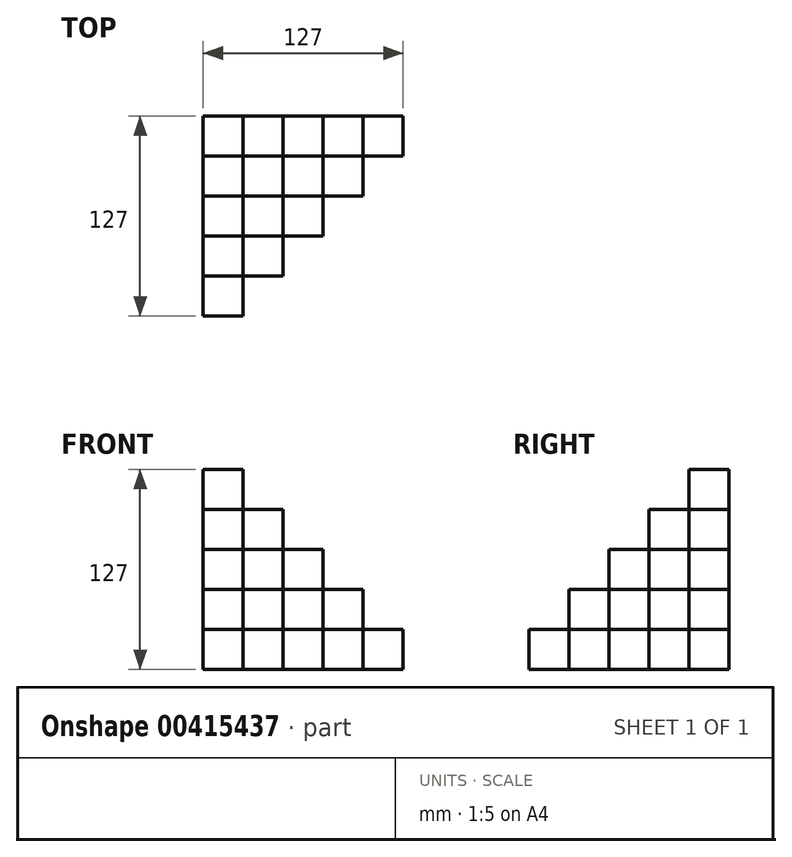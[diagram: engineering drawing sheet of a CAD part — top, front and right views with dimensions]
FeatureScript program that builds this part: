
annotation { "Feature Type Name" : "Feature", "Feature Type Description" : "" }
export const myFeature = defineFeature(function(context is Context, id is Id, definition is map)
    precondition{}
    {
        {
            var Q0;
            Q0=qCreatedBy(makeId("Top.planeOp"),FACE);
            var sketch = newSketch(context, id + "F0", { "sketchPlane" : qUnion([Q0])});
            skLineSegment(sketch, "E0.bottom", {"start": v(63.5, 63.5) * mm, "end": v(-63.5, 63.5) * mm, "construction": true});
            skLineSegment(sketch, "E0.top", {"start": v(63.5, -63.5) * mm, "end": v(-63.5, -63.5) * mm, "construction": true});
            skLineSegment(sketch, "E0.left", {"start": v(63.5, 63.5) * mm, "end": v(63.5, -63.5) * mm, "construction": true});
            skLineSegment(sketch, "E0.right", {"start": v(-63.5, 63.5) * mm, "end": v(-63.5, -63.5) * mm, "construction": true});
            skPoint(sketch, "E0.middle", {"position": v(0, 0) * mm});
            skLineSegment(sketch, "E1.bottom", {"start": v(-63.5, -63.5) * mm, "end": v(-38.1, -63.5) * mm});
            skLineSegment(sketch, "E1.top", {"start": v(-63.5, -38.1) * mm, "end": v(-38.1, -38.1) * mm});
            skLineSegment(sketch, "E1.left", {"start": v(-63.5, -63.5) * mm, "end": v(-63.5, -38.1) * mm});
            skLineSegment(sketch, "E1.right", {"start": v(-38.1, -63.5) * mm, "end": v(-38.1, -38.1) * mm});
            skLineSegment(sketch, "E2.bottom", {"start": v(-38.1, -38.1) * mm, "end": v(-12.7, -38.1) * mm});
            skLineSegment(sketch, "E2.top", {"start": v(-38.1, -12.7) * mm, "end": v(-12.7, -12.7) * mm});
            skLineSegment(sketch, "E2.left", {"start": v(-38.1, -38.1) * mm, "end": v(-38.1, -12.7) * mm});
            skLineSegment(sketch, "E2.right", {"start": v(-12.7, -38.1) * mm, "end": v(-12.7, -12.7) * mm});
            skLineSegment(sketch, "E3.bottom", {"start": v(-12.7, -12.7) * mm, "end": v(12.7, -12.7) * mm});
            skLineSegment(sketch, "E3.top", {"start": v(-12.7, 12.7) * mm, "end": v(12.7, 12.7) * mm});
            skLineSegment(sketch, "E3.left", {"start": v(-12.7, -12.7) * mm, "end": v(-12.7, 12.7) * mm});
            skLineSegment(sketch, "E3.right", {"start": v(12.7, -12.7) * mm, "end": v(12.7, 12.7) * mm});
            skLineSegment(sketch, "E4.bottom", {"start": v(12.7, 12.7) * mm, "end": v(38.1, 12.7) * mm});
            skLineSegment(sketch, "E4.top", {"start": v(12.7, 38.1) * mm, "end": v(38.1, 38.1) * mm});
            skLineSegment(sketch, "E4.left", {"start": v(12.7, 12.7) * mm, "end": v(12.7, 38.1) * mm});
            skLineSegment(sketch, "E4.right", {"start": v(38.1, 12.7) * mm, "end": v(38.1, 38.1) * mm});
            skLineSegment(sketch, "E5.bottom", {"start": v(38.1, 38.1) * mm, "end": v(63.5, 38.1) * mm});
            skLineSegment(sketch, "E5.top", {"start": v(38.1, 63.5) * mm, "end": v(63.5, 63.5) * mm});
            skLineSegment(sketch, "E5.left", {"start": v(38.1, 38.1) * mm, "end": v(38.1, 63.5) * mm});
            skLineSegment(sketch, "E5.right", {"start": v(63.5, 38.1) * mm, "end": v(63.5, 63.5) * mm});
            skSolve(sketch);
        }
        {
            var Q0;
            Q0=makeQuery(id+"F0.imprint","IMPRINT",FACE,{"disambiguationData":[TD([[makeQuery(id+"F0.imprint","IMPRINT",EDGE,{"derivedFrom":sQuery(id+"F0.wireOp",EDGE,"E2.bottom")}),1.0]])]});
            var Q1;
            Q1=makeQuery(id+"F0.imprint","IMPRINT",FACE,{"disambiguationData":[TD([[makeQuery(id+"F0.imprint","IMPRINT",EDGE,{"derivedFrom":sQuery(id+"F0.wireOp",EDGE,"E1.bottom")}),1.0]])]});
            var Q2;
            Q2=makeQuery(id+"F0.imprint","IMPRINT",FACE,{"disambiguationData":[TD([[makeQuery(id+"F0.imprint","IMPRINT",EDGE,{"derivedFrom":sQuery(id+"F0.wireOp",EDGE,"E3.bottom")}),1.0]])]});
            var Q3;
            Q3=makeQuery(id+"F0.imprint","IMPRINT",FACE,{"disambiguationData":[TD([[makeQuery(id+"F0.imprint","IMPRINT",EDGE,{"derivedFrom":sQuery(id+"F0.wireOp",EDGE,"E4.bottom")}),1.0]])]});
            var Q4;
            Q4=makeQuery(id+"F0.imprint","IMPRINT",FACE,{"disambiguationData":[TD([[makeQuery(id+"F0.imprint","IMPRINT",EDGE,{"derivedFrom":sQuery(id+"F0.wireOp",EDGE,"E5.bottom")}),1.0]])]});
            extrude(context, id + "F1", {"entities" : qUnion([Q0, Q1, Q2, Q3, Q4]), "depth" : 25.4 * mm});
        }
        {
            var Q0;
            Q0=qCreatedBy(makeId("Top.planeOp"),FACE);
            var sketch = newSketch(context, id + "F2", { "sketchPlane" : qUnion([Q0])});
            skLineSegment(sketch, "E6.bottom", {"start": v(63.5, 63.5) * mm, "end": v(-63.5, 63.5) * mm, "construction": true});
            skLineSegment(sketch, "E6.top", {"start": v(63.5, -63.5) * mm, "end": v(-63.5, -63.5) * mm, "construction": true});
            skLineSegment(sketch, "E6.left", {"start": v(63.5, 63.5) * mm, "end": v(63.5, -63.5) * mm, "construction": true});
            skLineSegment(sketch, "E6.right", {"start": v(-63.5, 63.5) * mm, "end": v(-63.5, -63.5) * mm, "construction": true});
            skPoint(sketch, "E6.middle", {"position": v(0, 0) * mm});
            skLineSegment(sketch, "E7", {"start": v(-63.5, -63.5) * mm, "end": v(-63.5, -38.1) * mm, "construction": true});
            skLineSegment(sketch, "E8", {"start": v(63.5, 63.5) * mm, "end": v(38.1, 63.5) * mm, "construction": true});
            skLineSegment(sketch, "E9.bottom", {"start": v(-63.5, -38.1) * mm, "end": v(-38.1, -38.1) * mm});
            skLineSegment(sketch, "E9.top", {"start": v(-63.5, -12.7) * mm, "end": v(-38.1, -12.7) * mm});
            skLineSegment(sketch, "E9.left", {"start": v(-63.5, -38.1) * mm, "end": v(-63.5, -12.7) * mm});
            skLineSegment(sketch, "E9.right", {"start": v(-38.1, -38.1) * mm, "end": v(-38.1, -12.7) * mm});
            skLineSegment(sketch, "E10.bottom", {"start": v(-38.1, -12.7) * mm, "end": v(-12.7, -12.7) * mm});
            skLineSegment(sketch, "E10.top", {"start": v(-38.1, 12.7) * mm, "end": v(-12.7, 12.7) * mm});
            skLineSegment(sketch, "E10.left", {"start": v(-38.1, -12.7) * mm, "end": v(-38.1, 12.7) * mm});
            skLineSegment(sketch, "E10.right", {"start": v(-12.7, -12.7) * mm, "end": v(-12.7, 12.7) * mm});
            skLineSegment(sketch, "E11.bottom", {"start": v(-12.7, 12.7) * mm, "end": v(12.7, 12.7) * mm});
            skLineSegment(sketch, "E11.top", {"start": v(-12.7, 38.1) * mm, "end": v(12.7, 38.1) * mm});
            skLineSegment(sketch, "E11.left", {"start": v(-12.7, 12.7) * mm, "end": v(-12.7, 38.1) * mm});
            skLineSegment(sketch, "E11.right", {"start": v(12.7, 12.7) * mm, "end": v(12.7, 38.1) * mm});
            skLineSegment(sketch, "E12.bottom", {"start": v(12.7, 38.1) * mm, "end": v(38.1, 38.1) * mm});
            skLineSegment(sketch, "E12.top", {"start": v(12.7, 63.5) * mm, "end": v(38.1, 63.5) * mm});
            skLineSegment(sketch, "E12.left", {"start": v(12.7, 38.1) * mm, "end": v(12.7, 63.5) * mm});
            skLineSegment(sketch, "E12.right", {"start": v(38.1, 38.1) * mm, "end": v(38.1, 63.5) * mm});
            skSolve(sketch);
        }
        {
            var Q0;
            Q0=qSketchRegion(id+"F2",true);
            extrude(context, id + "F3", {"entities" : qUnion([Q0]), "depth" : 50.8 * mm});
        }
        {
            var Q0;
            Q0=qCreatedBy(makeId("Top.planeOp"),FACE);
            var sketch = newSketch(context, id + "F4", { "sketchPlane" : qUnion([Q0])});
            skLineSegment(sketch, "E13.bottom", {"start": v(63.5, 63.5) * mm, "end": v(-63.5, 63.5) * mm, "construction": true});
            skLineSegment(sketch, "E13.top", {"start": v(63.5, -63.5) * mm, "end": v(-63.5, -63.5) * mm, "construction": true});
            skLineSegment(sketch, "E13.left", {"start": v(63.5, 63.5) * mm, "end": v(63.5, -63.5) * mm, "construction": true});
            skLineSegment(sketch, "E13.right", {"start": v(-63.5, 63.5) * mm, "end": v(-63.5, -63.5) * mm, "construction": true});
            skPoint(sketch, "E13.middle", {"position": v(0, 0) * mm});
            skLineSegment(sketch, "E14", {"start": v(-63.5, -63.5) * mm, "end": v(-63.5, -12.7) * mm, "construction": true});
            skLineSegment(sketch, "E15", {"start": v(63.5, 63.5) * mm, "end": v(12.7, 63.5) * mm, "construction": true});
            skLineSegment(sketch, "E16.bottom", {"start": v(12.7, 63.5) * mm, "end": v(-12.7, 63.5) * mm});
            skLineSegment(sketch, "E16.top", {"start": v(12.7, 38.1) * mm, "end": v(-12.7, 38.1) * mm});
            skLineSegment(sketch, "E16.left", {"start": v(12.7, 63.5) * mm, "end": v(12.7, 38.1) * mm});
            skLineSegment(sketch, "E16.right", {"start": v(-12.7, 63.5) * mm, "end": v(-12.7, 38.1) * mm});
            skLineSegment(sketch, "E17.bottom", {"start": v(-12.7, 38.1) * mm, "end": v(-38.1, 38.1) * mm});
            skLineSegment(sketch, "E17.top", {"start": v(-12.7, 12.7) * mm, "end": v(-38.1, 12.7) * mm});
            skLineSegment(sketch, "E17.left", {"start": v(-12.7, 38.1) * mm, "end": v(-12.7, 12.7) * mm});
            skLineSegment(sketch, "E17.right", {"start": v(-38.1, 38.1) * mm, "end": v(-38.1, 12.7) * mm});
            skLineSegment(sketch, "E18.bottom", {"start": v(-38.1, 12.7) * mm, "end": v(-63.5, 12.7) * mm});
            skLineSegment(sketch, "E18.top", {"start": v(-38.1, -12.7) * mm, "end": v(-63.5, -12.7) * mm});
            skLineSegment(sketch, "E18.left", {"start": v(-38.1, 12.7) * mm, "end": v(-38.1, -12.7) * mm});
            skLineSegment(sketch, "E18.right", {"start": v(-63.5, 12.7) * mm, "end": v(-63.5, -12.7) * mm});
            skSolve(sketch);
        }
        {
            var Q0;
            Q0=makeQuery(id+"F4.imprint","IMPRINT",FACE,{"disambiguationData":[TD([[makeQuery(id+"F4.imprint","IMPRINT",EDGE,{"derivedFrom":sQuery(id+"F4.wireOp",EDGE,"E18.bottom")}),1.0]])]});
            var Q1;
            Q1=makeQuery(id+"F4.imprint","IMPRINT",FACE,{"disambiguationData":[TD([[makeQuery(id+"F4.imprint","IMPRINT",EDGE,{"derivedFrom":sQuery(id+"F4.wireOp",EDGE,"E17.bottom")}),1.0]])]});
            var Q2;
            Q2=makeQuery(id+"F4.imprint","IMPRINT",FACE,{"disambiguationData":[TD([[makeQuery(id+"F4.imprint","IMPRINT",EDGE,{"derivedFrom":sQuery(id+"F4.wireOp",EDGE,"E16.bottom")}),1.0]])]});
            extrude(context, id + "F5", {"entities" : qUnion([Q0, Q1, Q2]), "depth" : 76.2 * mm});
        }
        {
            var Q0;
            Q0=qCreatedBy(makeId("Top.planeOp"),FACE);
            var sketch = newSketch(context, id + "F6", { "sketchPlane" : qUnion([Q0])});
            skLineSegment(sketch, "E19.bottom", {"start": v(63.5, 63.5) * mm, "end": v(-63.5, 63.5) * mm, "construction": true});
            skLineSegment(sketch, "E19.top", {"start": v(63.5, -63.5) * mm, "end": v(-63.5, -63.5) * mm, "construction": true});
            skLineSegment(sketch, "E19.left", {"start": v(63.5, 63.5) * mm, "end": v(63.5, -63.5) * mm, "construction": true});
            skLineSegment(sketch, "E19.right", {"start": v(-63.5, 63.5) * mm, "end": v(-63.5, -63.5) * mm, "construction": true});
            skPoint(sketch, "E19.middle", {"position": v(0, 0) * mm});
            skLineSegment(sketch, "E20", {"start": v(-63.5, 63.5) * mm, "end": v(-63.5, 12.7) * mm, "construction": true});
            skLineSegment(sketch, "E21", {"start": v(-63.5, 63.5) * mm, "end": v(-12.7, 63.5) * mm, "construction": true});
            skLineSegment(sketch, "E22.bottom", {"start": v(-63.5, 12.7) * mm, "end": v(-38.1, 12.7) * mm});
            skLineSegment(sketch, "E22.top", {"start": v(-63.5, 38.1) * mm, "end": v(-38.1, 38.1) * mm});
            skLineSegment(sketch, "E22.left", {"start": v(-63.5, 12.7) * mm, "end": v(-63.5, 38.1) * mm});
            skLineSegment(sketch, "E22.right", {"start": v(-38.1, 12.7) * mm, "end": v(-38.1, 38.1) * mm});
            skLineSegment(sketch, "E23.bottom", {"start": v(-38.1, 38.1) * mm, "end": v(-12.7, 38.1) * mm});
            skLineSegment(sketch, "E23.top", {"start": v(-38.1, 63.5) * mm, "end": v(-12.7, 63.5) * mm});
            skLineSegment(sketch, "E23.left", {"start": v(-38.1, 38.1) * mm, "end": v(-38.1, 63.5) * mm});
            skLineSegment(sketch, "E23.right", {"start": v(-12.7, 38.1) * mm, "end": v(-12.7, 63.5) * mm});
            skSolve(sketch);
        }
        {
            var Q0;
            Q0=makeQuery(id+"F6.imprint","IMPRINT",FACE,{"disambiguationData":[TD([[makeQuery(id+"F6.imprint","IMPRINT",EDGE,{"derivedFrom":sQuery(id+"F6.wireOp",EDGE,"E22.bottom")}),1.0]])]});
            var Q1;
            Q1=makeQuery(id+"F6.imprint","IMPRINT",FACE,{"disambiguationData":[TD([[makeQuery(id+"F6.imprint","IMPRINT",EDGE,{"derivedFrom":sQuery(id+"F6.wireOp",EDGE,"E23.bottom")}),1.0]])]});
            extrude(context, id + "F7", {"entities" : qUnion([Q0, Q1]), "depth" : 101.6 * mm});
        }
        {
            var Q0;
            Q0=qCreatedBy(makeId("Top.planeOp"),FACE);
            var sketch = newSketch(context, id + "F8", { "sketchPlane" : qUnion([Q0])});
            skLineSegment(sketch, "E24.bottom", {"start": v(63.5, 63.5) * mm, "end": v(-63.5, 63.5) * mm, "construction": true});
            skLineSegment(sketch, "E24.top", {"start": v(63.5, -63.5) * mm, "end": v(-63.5, -63.5) * mm, "construction": true});
            skLineSegment(sketch, "E24.left", {"start": v(63.5, 63.5) * mm, "end": v(63.5, -63.5) * mm, "construction": true});
            skLineSegment(sketch, "E24.right", {"start": v(-63.5, 63.5) * mm, "end": v(-63.5, -63.5) * mm, "construction": true});
            skPoint(sketch, "E24.middle", {"position": v(0, 0) * mm});
            skLineSegment(sketch, "E25.bottom", {"start": v(-63.5, 63.5) * mm, "end": v(-38.1, 63.5) * mm});
            skLineSegment(sketch, "E25.top", {"start": v(-63.5, 38.1) * mm, "end": v(-38.1, 38.1) * mm});
            skLineSegment(sketch, "E25.left", {"start": v(-63.5, 63.5) * mm, "end": v(-63.5, 38.1) * mm});
            skLineSegment(sketch, "E25.right", {"start": v(-38.1, 63.5) * mm, "end": v(-38.1, 38.1) * mm});
            skSolve(sketch);
        }
        {
            var Q0;
            Q0=makeQuery(id+"F8.imprint","IMPRINT",FACE,{"disambiguationData":[TD([[makeQuery(id+"F8.imprint","IMPRINT",EDGE,{"derivedFrom":sQuery(id+"F8.wireOp",EDGE,"E25.bottom")}),-1.0]])]});
            extrude(context, id + "F9", {"entities" : qUnion([Q0]), "depth" : 127 * mm});
        }
    });
